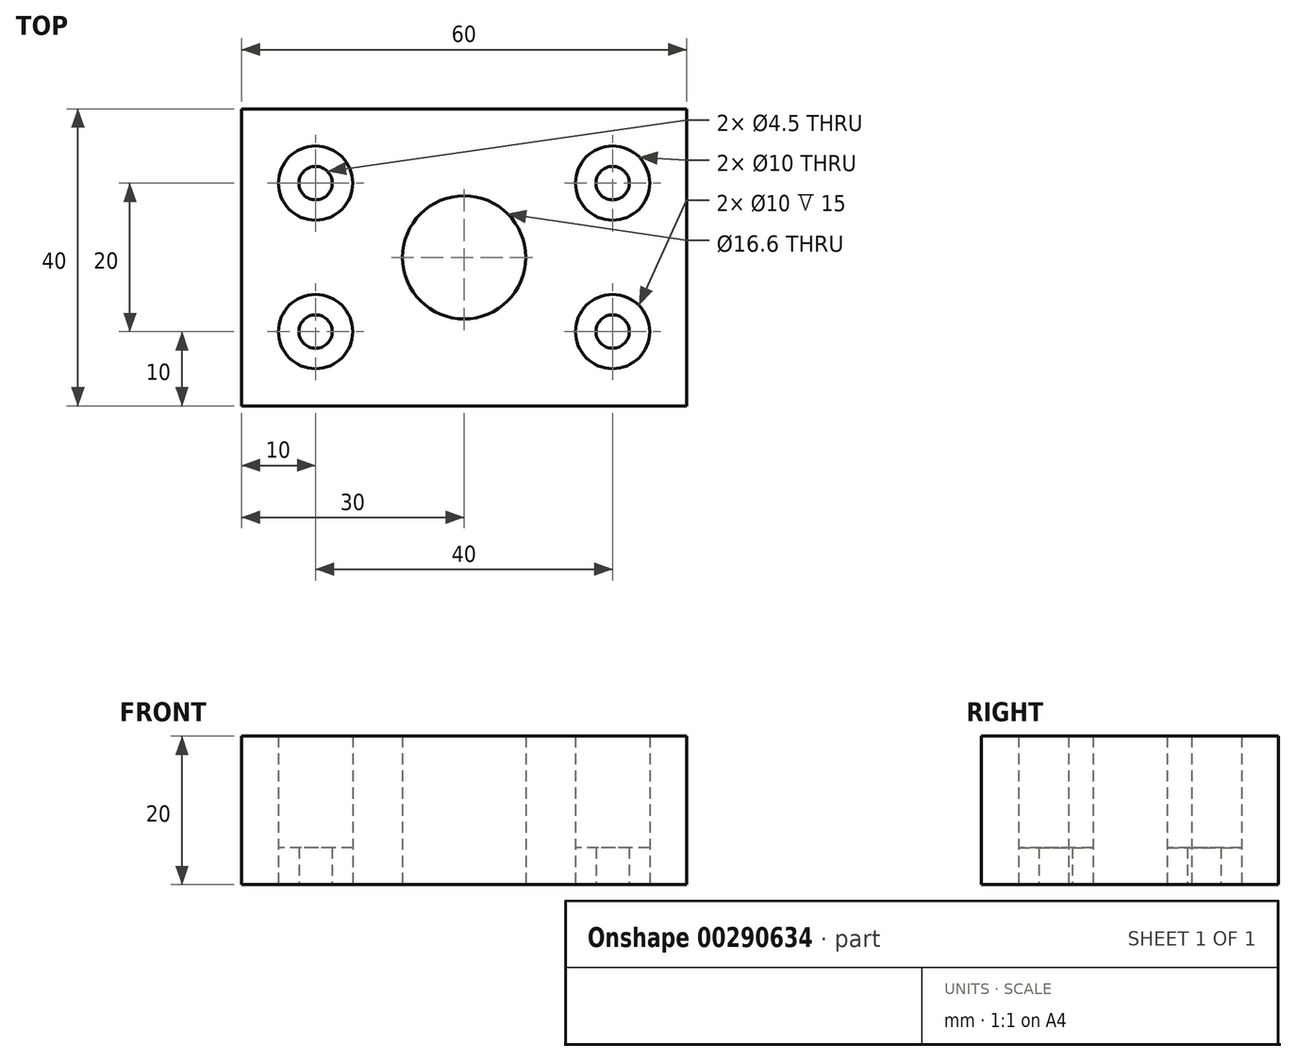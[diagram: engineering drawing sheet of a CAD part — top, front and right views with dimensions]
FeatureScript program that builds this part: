
annotation { "Feature Type Name" : "Feature", "Feature Type Description" : "" }
export const myFeature = defineFeature(function(context is Context, id is Id, definition is map)
    precondition{}
    {
        {
            var Q0;
            Q0=qCreatedBy(makeId("Top.planeOp"),FACE);
            var sketch = newSketch(context, id + "F0", { "sketchPlane" : qUnion([Q0])});
            skCircle(sketch, "E0", {"center": v(0, 0) * mm, "radius": 8.3 * mm});
            skLineSegment(sketch, "E1.bottom", {"start": v(-30, 20) * mm, "end": v(30, 20) * mm});
            skLineSegment(sketch, "E1.top", {"start": v(-30, -20) * mm, "end": v(30, -20) * mm});
            skLineSegment(sketch, "E1.left", {"start": v(-30, 20) * mm, "end": v(-30, -20) * mm});
            skLineSegment(sketch, "E1.right", {"start": v(30, 20) * mm, "end": v(30, -20) * mm});
            skLineSegment(sketch, "E2", {"start": v(0, 20) * mm, "end": v(0, -20) * mm, "construction": true});
            skPoint(sketch, "E2.endSnap0", {"position": v(0, -20) * mm});
            skLineSegment(sketch, "E3", {"start": v(-30, 10) * mm, "end": v(30, 10) * mm, "construction": true});
            skLineSegment(sketch, "E4", {"start": v(-20, 20) * mm, "end": v(-20, -20) * mm, "construction": true});
            skCircle(sketch, "E5", {"center": v(-20, 10) * mm, "radius": 2.25 * mm});
            skLineSegment(sketch, "E6", {"start": v(-30, 0) * mm, "end": v(30, 0) * mm, "construction": true});
            skLineSegment(sketch, "E7", {"start": v(-30, -10) * mm, "end": v(30, -10) * mm, "construction": true});
            skCircle(sketch, "E8.MirrorC", {"center": v(20, 10) * mm, "radius": 2.25 * mm});
            skLineSegment(sketch, "E9.MirrorCS", {"start": v(30, 10) * mm, "end": v(-30, 10) * mm, "construction": true});
            skCircle(sketch, "E10.MirrorC", {"center": v(-20, -10) * mm, "radius": 2.25 * mm});
            skCircle(sketch, "E11.MirrorC", {"center": v(20, -10) * mm, "radius": 2.25 * mm});
            skCircle(sketch, "E12", {"center": v(-20, 10) * mm, "radius": 5 * mm});
            skCircle(sketch, "E13.MirrorC", {"center": v(20, 10) * mm, "radius": 5 * mm});
            skCircle(sketch, "E14.MirrorC", {"center": v(-20, -10) * mm, "radius": 5 * mm});
            skCircle(sketch, "E15.MirrorC", {"center": v(20, -10) * mm, "radius": 5 * mm});
            skSolve(sketch);
        }
        {
            var Q0;
            Q0=qSketchRegion(id+"F0",true);
            var Q1;
            Q1=makeQuery(id+"F0.imprint","IMPRINT",FACE,{"disambiguationData":[TD([[makeQuery(id+"F0.imprint","IMPRINT",EDGE,{"derivedFrom":sQuery(id+"F0.wireOp",EDGE,"E5")}),-1.0]])]});
            var Q2;
            Q2=makeQuery(id+"F0.imprint","IMPRINT",FACE,{"disambiguationData":[TD([[makeQuery(id+"F0.imprint","IMPRINT",EDGE,{"derivedFrom":sQuery(id+"F0.wireOp",EDGE,"E8.MirrorC")}),1.0]])]});
            var Q3;
            Q3=makeQuery(id+"F0.imprint","IMPRINT",FACE,{"disambiguationData":[TD([[makeQuery(id+"F0.imprint","IMPRINT",EDGE,{"derivedFrom":sQuery(id+"F0.wireOp",EDGE,"E11.MirrorC")}),-1.0]])]});
            var Q4;
            Q4=makeQuery(id+"F0.imprint","IMPRINT",FACE,{"disambiguationData":[TD([[makeQuery(id+"F0.imprint","IMPRINT",EDGE,{"derivedFrom":sQuery(id+"F0.wireOp",EDGE,"E10.MirrorC")}),1.0]])]});
            extrude(context, id + "F1", {"entities" : qUnion([Q0, Q1, Q2, Q3, Q4]), "depth" : 20 * mm});
        }
        {
            var Q0;
            Q0=makeQuery(id+"F0.imprint","IMPRINT",FACE,{"disambiguationData":[TD([[makeQuery(id+"F0.imprint","IMPRINT",EDGE,{"derivedFrom":sQuery(id+"F0.wireOp",EDGE,"E10.MirrorC")}),1.0]])]});
            var Q1;
            Q1=makeQuery(id+"F0.imprint","IMPRINT",FACE,{"disambiguationData":[TD([[makeQuery(id+"F0.imprint","IMPRINT",EDGE,{"derivedFrom":sQuery(id+"F0.wireOp",EDGE,"E11.MirrorC")}),-1.0]])]});
            var Q2;
            Q2=makeQuery(id+"F0.imprint","IMPRINT",FACE,{"disambiguationData":[TD([[makeQuery(id+"F0.imprint","IMPRINT",EDGE,{"derivedFrom":sQuery(id+"F0.wireOp",EDGE,"E5")}),-1.0]])]});
            var Q3;
            Q3=makeQuery(id+"F0.imprint","IMPRINT",FACE,{"disambiguationData":[TD([[makeQuery(id+"F0.imprint","IMPRINT",EDGE,{"derivedFrom":sQuery(id+"F0.wireOp",EDGE,"E8.MirrorC")}),1.0]])]});
            extrude(context, id + "F2", {"entities" : qUnion([Q0, Q1, Q2, Q3]), "operationType" : NewBodyOperationType.REMOVE, "depth" : 20 * mm, "hasSecondDirection" : true, "secondDirectionOppositeDirection" : false, "secondDirectionDepth" : 5 * mm});
        }
    });
